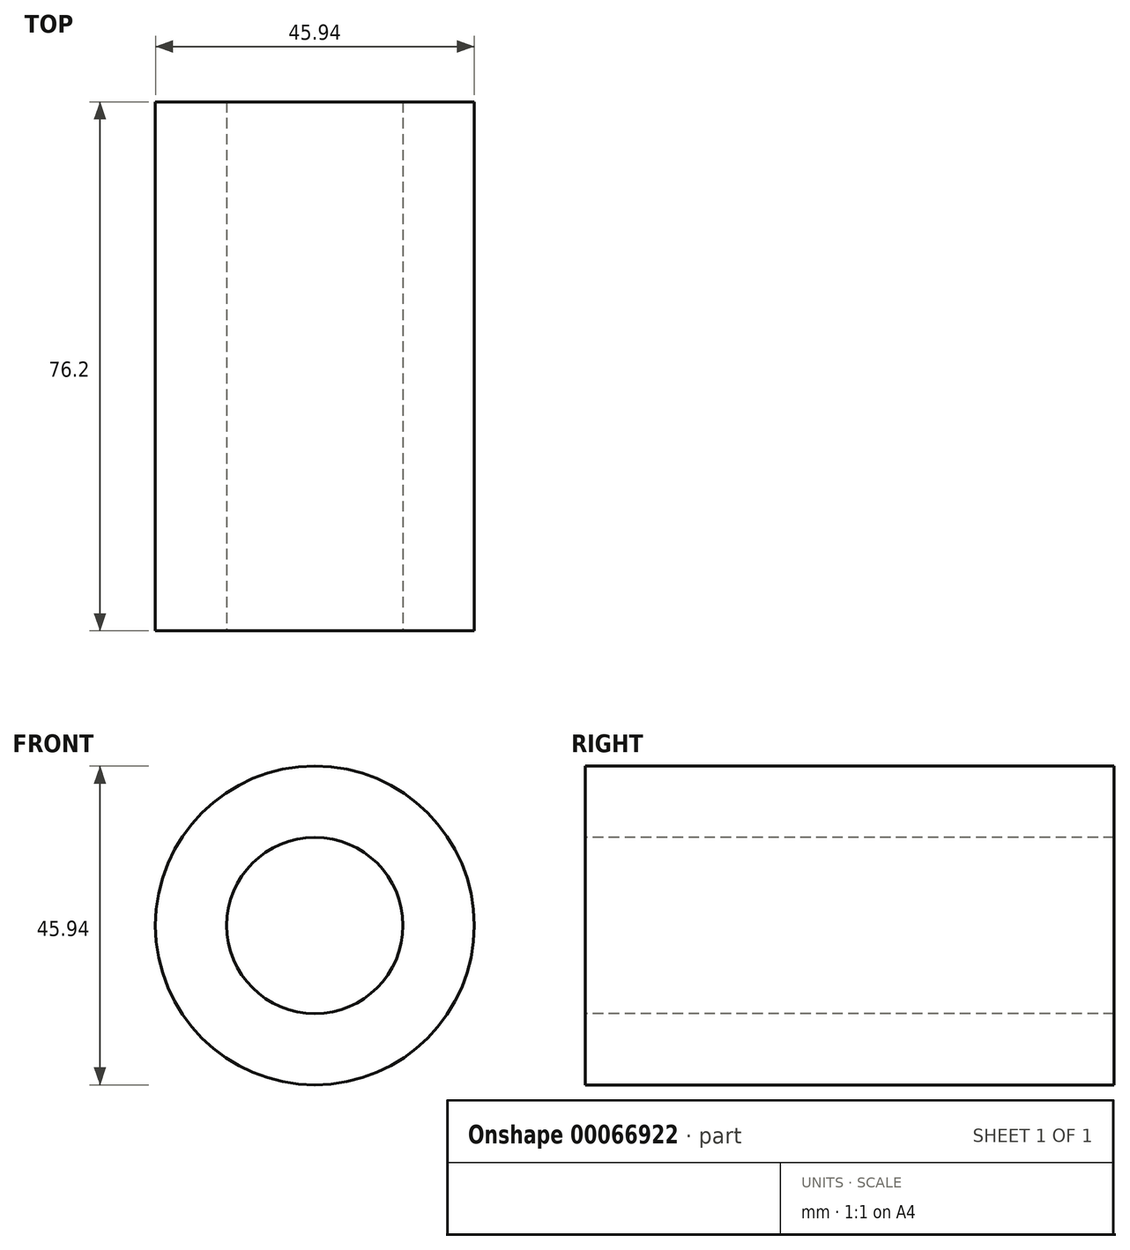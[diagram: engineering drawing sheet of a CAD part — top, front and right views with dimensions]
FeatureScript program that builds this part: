
annotation { "Feature Type Name" : "Feature", "Feature Type Description" : "" }
export const myFeature = defineFeature(function(context is Context, id is Id, definition is map)
    precondition{}
    {
        {
            var Q0;
            Q0=qCreatedBy(makeId("Front.planeOp"),FACE);
            var sketch = newSketch(context, id + "F0", { "sketchPlane" : qUnion([Q0])});
            skCircle(sketch, "E0", {"center": v(0, 0) * mm, "radius": 22.97 * mm});
            skSolve(sketch);
        }
        {
            var Q0;
            Q0=makeQuery(id+"F0.imprint","IMPRINT",FACE,{"disambiguationData":[TD([[makeQuery(id+"F0.imprint","IMPRINT",EDGE,{"derivedFrom":sQuery(id+"F0.wireOp",EDGE,"E0")}),1.0]])]});
            extrude(context, id + "F1", {"entities" : qUnion([Q0]), "depth" : 76.2 * mm});
        }
        {
            var Q0;
            Q0=makeQuery(id+"F1.opExtrude","CAP_FACE",FACE,{"disambiguationData":[OSD([sQuery(id+"F0.wireOp",EDGE,"E0")])],"isStart":false});
            var sketch = newSketch(context, id + "F2", { "sketchPlane" : qUnion([Q0])});
            skCircle(sketch, "E1", {"center": v(0, 0) * mm, "radius": 12.76 * mm});
            skSolve(sketch);
        }
        {
            var Q0;
            Q0=sQuery(id+"F2.wireOp",VERTEX,"E1.center");
            var Q1;
            Q1=makeQuery(id+"F1.opExtrude","SWEPT_BODY",BODY,{"disambiguationData":[OSD([sQuery(id+"F0.wireOp",EDGE,"E0")])]});
            hole(context, id + "F3", {"style" : HoleStyle.SIMPLE, "holeDiameter" : 25.4 * mm, "endStyle" : HoleEndStyle.THROUGH, "locations" : qUnion([Q0]), "scope" : qUnion([Q1])});
        }
    });
